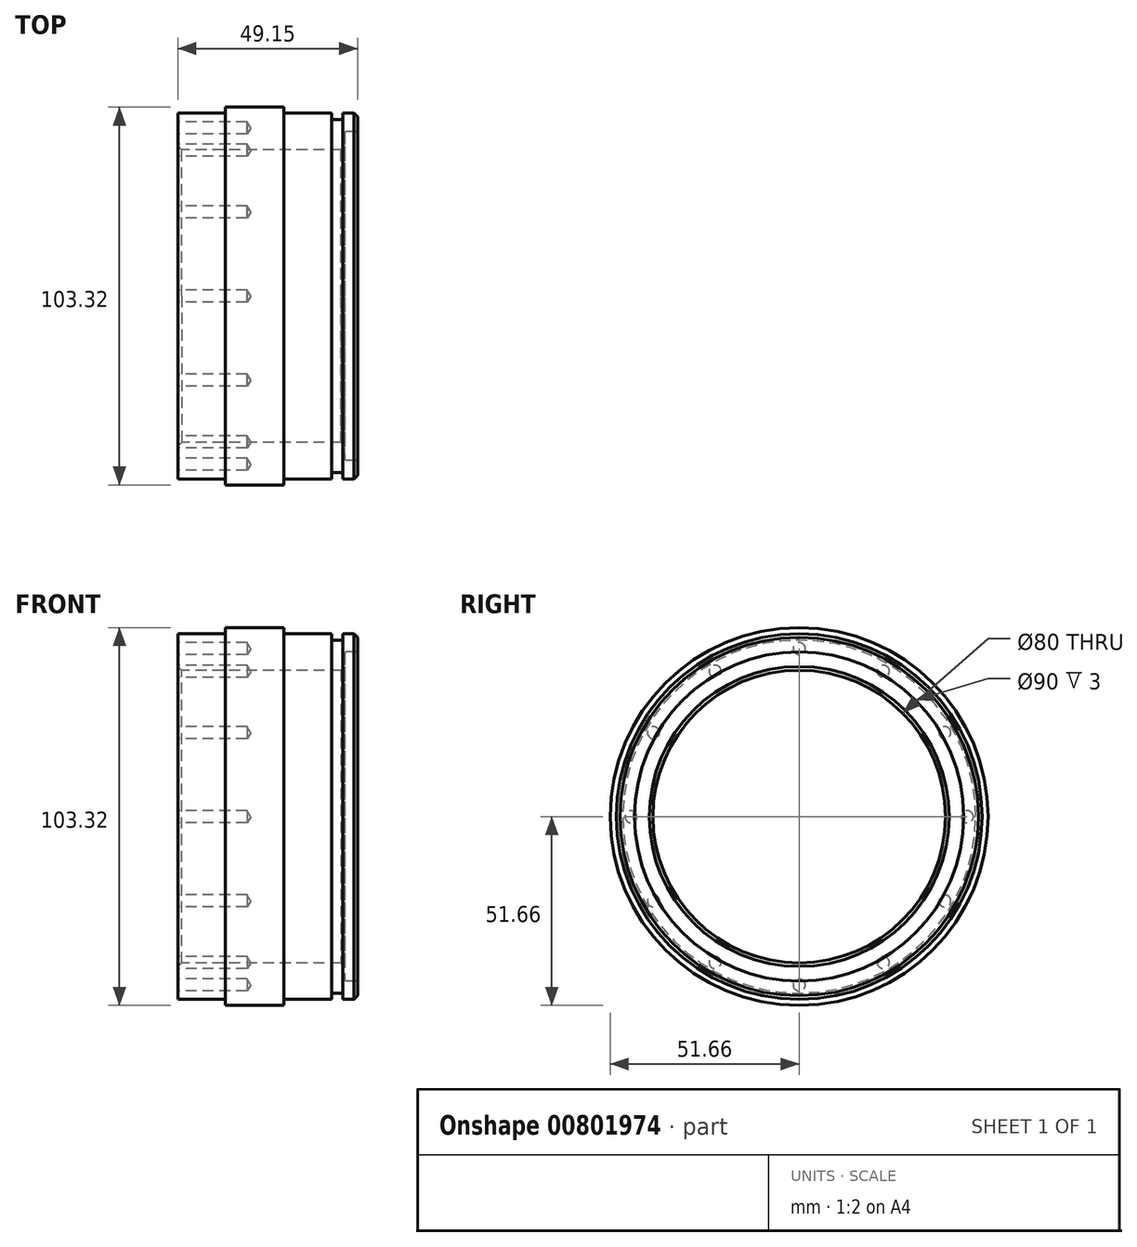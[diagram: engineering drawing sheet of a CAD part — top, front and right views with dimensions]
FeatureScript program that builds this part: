
annotation { "Feature Type Name" : "Feature", "Feature Type Description" : "" }
export const myFeature = defineFeature(function(context is Context, id is Id, definition is map)
    precondition{}
    {
        {
            var Q0;
            Q0=qCreatedBy(makeId("Front.planeOp"),FACE);
            var sketch = newSketch(context, id + "F0", { "sketchPlane" : qUnion([Q0])});
            skLineSegment(sketch, "E0", {"start": v(-26.06, -44.48) * mm, "end": v(52.5, -44.48) * mm, "construction": true});
            skLineSegment(sketch, "E1", {"start": v(-30.1, 5.52) * mm, "end": v(-30.1, -4.48) * mm});
            skLineSegment(sketch, "E2", {"start": v(-30.1, 5.52) * mm, "end": v(-17.6, 5.52) * mm});
            skLineSegment(sketch, "E3", {"start": v(-17.1, 6.02) * mm, "end": v(-17.1, 7.18) * mm});
            skLineSegment(sketch, "E4", {"start": v(-17.1, 7.18) * mm, "end": v(-1.1, 7.18) * mm});
            skLineSegment(sketch, "E5", {"start": v(-1.1, 7.18) * mm, "end": v(-1.1, 6.02) * mm});
            skLineSegment(sketch, "E6", {"start": v(-0.6, 5.52) * mm, "end": v(11.9, 5.52) * mm});
            skLineSegment(sketch, "E7", {"start": v(11.9, 5.52) * mm, "end": v(11.9, 3.77) * mm});
            skLineSegment(sketch, "E8", {"start": v(11.9, 3.77) * mm, "end": v(15.05, 3.77) * mm});
            skLineSegment(sketch, "E9", {"start": v(15.05, 3.77) * mm, "end": v(15.05, 5.52) * mm});
            skLineSegment(sketch, "E10", {"start": v(15.05, 5.52) * mm, "end": v(19.05, 5.52) * mm});
            skLineSegment(sketch, "E11", {"start": v(19.05, 5.52) * mm, "end": v(19.05, 0.52) * mm});
            skLineSegment(sketch, "E12", {"start": v(15.55, -4.48) * mm, "end": v(-30.1, -4.48) * mm});
            skLineSegment(sketch, "E13.top", {"start": v(19.05, 0.52) * mm, "end": v(16.05, 0.52) * mm});
            skLineSegment(sketch, "E13.right", {"start": v(15.55, -4.48) * mm, "end": v(15.55, 0.02) * mm});
            skPoint(sketch, "E14.visualSharp", {"position": v(15.55, 0.52) * mm});
            skArc(sketch, "E14.filletArc", {"start": v(16.05, 0.52) * mm, "mid": v(15.7, 0.37) * mm, "end": v(15.55, 0.02) * mm});
            skPoint(sketch, "E15.visualSharp", {"position": v(-1.1, 5.52) * mm});
            skArc(sketch, "E15.filletArc", {"start": v(-1.1, 6.02) * mm, "mid": v(-0.95, 5.66) * mm, "end": v(-0.6, 5.52) * mm});
            skPoint(sketch, "E16.visualSharp", {"position": v(-17.1, 5.52) * mm});
            skArc(sketch, "E16.filletArc", {"start": v(-17.6, 5.52) * mm, "mid": v(-17.24, 5.66) * mm, "end": v(-17.1, 6.02) * mm});
            skSolve(sketch);
        }
        {
            var Q0;
            Q0=qSketchRegion(id+"F0",true);
            var Q1;
            Q1=sQuery(id+"F0.wireOp",EDGE,"E0");
            revolve(context, id + "F1", {"entities" : qUnion([Q0]), "axis" : qUnion([Q1]), "revolveType" : RevolveType.FULL});
        }
        {
            var Q0;
            Q0=makeQuery(id+"F1.opRevolve","SWEPT_BODY",BODY,{"disambiguationData":[OSD([sQuery(id+"F0.wireOp",EDGE,"E1"),sQuery(id+"F0.wireOp",EDGE,"E2"),sQuery(id+"F0.wireOp",EDGE,"E3"),sQuery(id+"F0.wireOp",EDGE,"E4"),sQuery(id+"F0.wireOp",EDGE,"E5"),sQuery(id+"F0.wireOp",EDGE,"E6"),sQuery(id+"F0.wireOp",EDGE,"E7"),sQuery(id+"F0.wireOp",EDGE,"E8"),sQuery(id+"F0.wireOp",EDGE,"E9"),sQuery(id+"F0.wireOp",EDGE,"E10"),sQuery(id+"F0.wireOp",EDGE,"E11"),sQuery(id+"F0.wireOp",EDGE,"E12")])]});
            transform(context, id + "F2", {"entities" : qUnion([Q0]), "transformType" : TransformType.TRANSLATION_3D, "dx" : 0 * mm, "dy" : 0 * mm, "dz" : 44.56 * mm, "makeCopy" : false});
        }
        {
            var Q0;
            Q0=makeQuery(id+"F1.opRevolve","SWEPT_FACE",FACE,{"disambiguationData":[OSD([sQuery(id+"F0.wireOp",EDGE,"E1")])]});
            var sketch = newSketch(context, id + "F3", { "sketchPlane" : qUnion([Q0])});
            skLineSegment(sketch, "E17", {"start": v(0, 0) * mm, "end": v(0, 46) * mm, "construction": true});
            skPoint(sketch, "E18", {"position": v(0, 46) * mm});
            skPoint(sketch, "E19.1.0", {"position": v(-23, 39.84) * mm});
            skPoint(sketch, "E19.2.0", {"position": v(-39.84, 23) * mm});
            skPoint(sketch, "E19.3.0", {"position": v(-46, 0) * mm});
            skPoint(sketch, "E19.4.0", {"position": v(-39.84, -23) * mm});
            skPoint(sketch, "E19.5.0", {"position": v(-23, -39.84) * mm});
            skPoint(sketch, "E19.6.0", {"position": v(0, -46) * mm});
            skPoint(sketch, "E19.7.0", {"position": v(23, -39.84) * mm});
            skPoint(sketch, "E19.8.0", {"position": v(39.84, -23) * mm});
            skPoint(sketch, "E19.9.0", {"position": v(46, 0) * mm});
            skPoint(sketch, "E19.10.0", {"position": v(39.84, 23) * mm});
            skPoint(sketch, "E19.11.0", {"position": v(23, 39.84) * mm});
            skPoint(sketch, "E19.center", {"position": v(0, 0) * mm});
            skSolve(sketch);
        }
        {
            var Q0;
            Q0=sQuery(id+"F3.wireOp",VERTEX,"E18");
            var Q1;
            Q1=sQuery(id+"F3.wireOp",VERTEX,"E19.11.0");
            var Q2;
            Q2=sQuery(id+"F3.wireOp",VERTEX,"E19.10.0");
            var Q3;
            Q3=sQuery(id+"F3.wireOp",VERTEX,"E19.9.0");
            var Q4;
            Q4=sQuery(id+"F3.wireOp",VERTEX,"E19.8.0");
            var Q5;
            Q5=sQuery(id+"F3.wireOp",VERTEX,"E19.7.0");
            var Q6;
            Q6=sQuery(id+"F3.wireOp",VERTEX,"E19.6.0");
            var Q7;
            Q7=sQuery(id+"F3.wireOp",VERTEX,"E19.5.0");
            var Q8;
            Q8=sQuery(id+"F3.wireOp",VERTEX,"E19.4.0");
            var Q9;
            Q9=sQuery(id+"F3.wireOp",VERTEX,"E19.3.0");
            var Q10;
            Q10=sQuery(id+"F3.wireOp",VERTEX,"E19.2.0");
            var Q11;
            Q11=sQuery(id+"F3.wireOp",VERTEX,"E19.1.0");
            var Q12;
            Q12=makeQuery(id+"F1.opRevolve","SWEPT_BODY",BODY,{"disambiguationData":[OSD([sQuery(id+"F0.wireOp",EDGE,"E1"),sQuery(id+"F0.wireOp",EDGE,"E2"),sQuery(id+"F0.wireOp",EDGE,"E3"),sQuery(id+"F0.wireOp",EDGE,"E4"),sQuery(id+"F0.wireOp",EDGE,"E5"),sQuery(id+"F0.wireOp",EDGE,"E6"),sQuery(id+"F0.wireOp",EDGE,"E7"),sQuery(id+"F0.wireOp",EDGE,"E8"),sQuery(id+"F0.wireOp",EDGE,"E9"),sQuery(id+"F0.wireOp",EDGE,"E10"),sQuery(id+"F0.wireOp",EDGE,"E11"),sQuery(id+"F0.wireOp",EDGE,"E12")])]});
            hole(context, id + "F4", {"style" : HoleStyle.SIMPLE, "endStyle" : HoleEndStyle.BLIND, "standardTappedOrClearance" : lookupTablePath({ "standard" : "ISO", "engagement" : "75%", "pitch" : "0.7 mm", "size" : "M4", "type" : "Tapped" }), "standardBlindInLast" : lookupTablePath({ "standard" : "ISO", "engagement" : "75%", "pitch" : "0.7 mm", "size" : "M4", "type" : "Tapped" }), "holeDiameter" : 3.3 * mm, "showTappedDepth" : true, "holeDepth" : 18.93 * mm, "tappedDepth" : 16.82 * mm, "tapClearance" : 3, "startFromSketch" : true, "locations" : qUnion([Q0, Q1, Q2, Q3, Q4, Q5, Q6, Q7, Q8, Q9, Q10, Q11]), "scope" : qUnion([Q12]), "majorDiameter" : 4 * mm});
        }
        {
            var Q0;
            Q0=makeQuery(id+"F1.opRevolve","SWEPT_FACE",FACE,{"disambiguationData":[OSD([sQuery(id+"F0.wireOp",EDGE,"E12")])]});
            var Q1;
            Q1=makeQuery(id+"F1.opRevolve","SWEPT_EDGE",EDGE,{"disambiguationData":[OSD([sQuery(id+"F0.wireOp",EDGE,"E10"),sQuery(id+"F0.wireOp",EDGE,"E11")])]});
            chamfer(context, id + "F5", {"entities" : qUnion([Q0, Q1]), "width" : 1 * mm, "tangentPropagation" : true});
        }
    });
